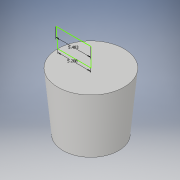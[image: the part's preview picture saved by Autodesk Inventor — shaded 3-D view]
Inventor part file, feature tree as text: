
AUTODESK INVENTOR PART (.ipt)
format: ipt  version: 2017 (Build 210142000, 142)  size: 97,792 bytes
history: native  units: in
note: dims shown in document units (in); Inventor stores cm internally (conversion verified against a paired STEP export)
features: revolve x1, sketch x1
ambient origin geometry x8: Origin, YZ Plane, XZ Plane, XY Plane, X Axis, Y Axis, Z Axis, Center Point
bodies: Body1 (feature_tree)
feature tree (2):
  revolve  "Revolution2"  [1 undecoded]
  sketch  "Sketch2"  dims[d2=5.4825in d9=5.2084in d11=90.0deg]
note: 1 required parameter value undecoded (feature->parameter linkage not recoverable at this tier; creation-order binding heuristic only, values carry confidence <= 0.55)
